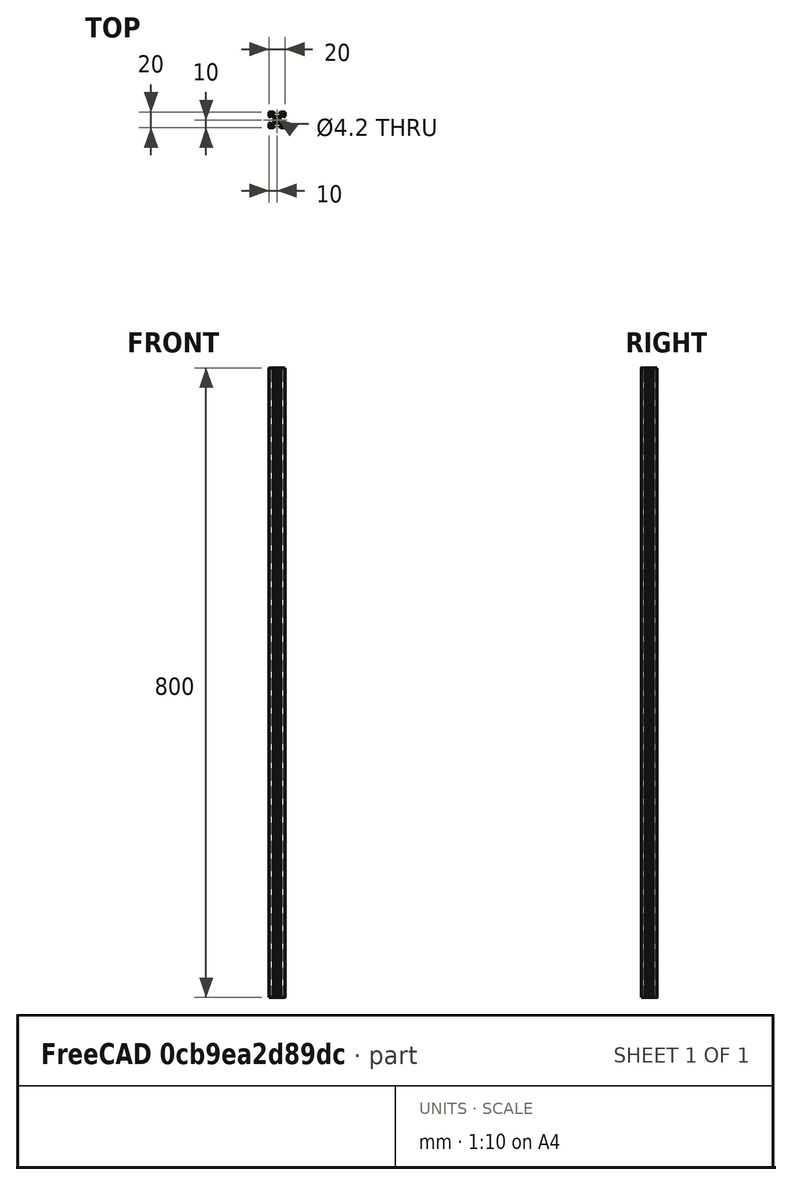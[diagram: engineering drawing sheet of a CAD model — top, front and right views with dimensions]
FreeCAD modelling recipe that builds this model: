
FCSTD DOCUMENT  (FreeCAD 0.19R)
Label: 2020-800
License: All rights reserved
LicenseURL: http://en.wikipedia.org/wiki/All_rights_reserved
objects: Sketcher::SketchObject×1, PartDesign::Pad×1, PartDesign::Body×1
note: 4 computed .brp shape members not serialized (recipe doc carries the construction recipe); baked Part::Feature solids carry a one-line shape summary decoded from their .brp

FEATURE [Sketcher::SketchObject] Sketch
  FullyConstrained = true
  MapMode = 5
  Support = -> [XY_Plane]
  sketch-geometry (65):
    g0: LineSegment StartX=-10 StartY=4.58 StartZ=0 EndX=-10 EndY=9.5 EndZ=0
    g1: LineSegment StartX=-9.5 StartY=10 StartZ=0 EndX=-4.58 EndY=10 EndZ=0
    g2: LineSegment StartX=-5.5 StartY=8.2 StartZ=0 EndX=-3.125 EndY=8.2 EndZ=0
    g3: LineSegment StartX=-8.2 StartY=5.5 StartZ=0 EndX=-8.2 EndY=3.125 EndZ=0
    g4: LineSegment StartX=-0.125 StartY=3.9 StartZ=0 EndX=-2.83934 EndY=3.9 EndZ=0
    g5: LineSegment StartX=-3.9 StartY=2.83934 StartZ=0 EndX=-3.9 EndY=0.125 EndZ=0
    g6: ArcOfCircle CenterX=0 CenterY=3.9 CenterZ=0 NormalX=0 NormalY=0 NormalZ=1 AngleXU=0 Radius=0.125 StartAngle=3.14159 EndAngle=6.28319
    g7: ArcOfCircle CenterX=-3.9 CenterY=0 CenterZ=0 NormalX=0 NormalY=0 NormalZ=1 AngleXU=0 Radius=0.125 StartAngle=4.71239 EndAngle=7.85398
    g8: ArcOfCircle CenterX=-9.5 CenterY=9.5 CenterZ=0 NormalX=0 NormalY=0 NormalZ=1 AngleXU=0 Radius=0.5 StartAngle=1.5708 EndAngle=3.14159
    g9: LineSegment StartX=-5.5 StartY=8.2 StartZ=0 EndX=-5.5 EndY=6.56066 EndZ=0
    g10: LineSegment StartX=-8.2 StartY=5.5 StartZ=0 EndX=-6.56066 EndY=5.5 EndZ=0
    g11: LineSegment StartX=-4.58 StartY=10 StartZ=0 EndX=-3.125 EndY=8.545 EndZ=0
    g12: LineSegment StartX=-3.125 StartY=8.545 StartZ=0 EndX=-3.125 EndY=8.2 EndZ=0
    g13: LineSegment StartX=-10 StartY=4.58 StartZ=0 EndX=-8.545 EndY=3.125 EndZ=0
    g14: LineSegment StartX=-8.545 StartY=3.125 StartZ=0 EndX=-8.2 EndY=3.125 EndZ=0
    g15: LineSegment StartX=-5.5 StartY=6.56066 StartZ=0 EndX=-2.83934 EndY=3.9 EndZ=0
    g16: LineSegment StartX=-6.56066 StartY=5.5 StartZ=0 EndX=-3.9 EndY=2.83934 EndZ=0
    g17: Circle CenterX=0 CenterY=0 CenterZ=0 NormalX=0 NormalY=0 NormalZ=1 AngleXU=0 Radius=2.1
    g18: LineSegment StartX=0.125 StartY=3.9 StartZ=0 EndX=2.83934 EndY=3.9 EndZ=0
    g19: LineSegment StartX=2.83934 StartY=3.9 StartZ=0 EndX=5.5 EndY=6.56066 EndZ=0
    g20: LineSegment StartX=5.5 StartY=6.56066 StartZ=0 EndX=5.5 EndY=8.2 EndZ=0
    g21: LineSegment StartX=3.125 StartY=8.2 StartZ=0 EndX=3.125 EndY=8.545 EndZ=0
    g22: LineSegment StartX=5.5 StartY=8.2 StartZ=0 EndX=3.125 EndY=8.2 EndZ=0
    g23: LineSegment StartX=4.58 StartY=10 StartZ=0 EndX=9.5 EndY=10 EndZ=0
    g24: ArcOfCircle CenterX=9.5 CenterY=9.5 CenterZ=0 NormalX=0 NormalY=0 NormalZ=1 AngleXU=0 Radius=0.5 StartAngle=1.9e-15 EndAngle=1.5708
    g25: LineSegment StartX=10 StartY=9.5 StartZ=0 EndX=10 EndY=4.58 EndZ=0
    g26: LineSegment StartX=10 StartY=4.58 StartZ=0 EndX=8.545 EndY=3.125 EndZ=0
    g27: LineSegment StartX=8.545 StartY=3.125 StartZ=0 EndX=8.2 EndY=3.125 EndZ=0
    g28: LineSegment StartX=8.2 StartY=3.125 StartZ=0 EndX=8.2 EndY=5.5 EndZ=0
    g29: LineSegment StartX=8.2 StartY=5.5 StartZ=0 EndX=6.56066 EndY=5.5 EndZ=0
    g30: LineSegment StartX=6.56066 StartY=5.5 StartZ=0 EndX=3.9 EndY=2.83934 EndZ=0
    g31: LineSegment StartX=3.9 StartY=2.83934 StartZ=0 EndX=3.9 EndY=0.125 EndZ=0
    g32: ArcOfCircle CenterX=3.9 CenterY=0 CenterZ=0 NormalX=0 NormalY=0 NormalZ=1 AngleXU=0 Radius=0.125 StartAngle=1.5708 EndAngle=4.71239
    g33: LineSegment StartX=3.9 StartY=-0.125 StartZ=0 EndX=3.9 EndY=-2.83934 EndZ=0
    g34: LineSegment StartX=3.9 StartY=-2.83934 StartZ=0 EndX=6.56066 EndY=-5.5 EndZ=0
    g35: LineSegment StartX=6.56066 StartY=-5.5 StartZ=0 EndX=8.2 EndY=-5.5 EndZ=0
    g36: LineSegment StartX=8.2 StartY=-5.5 StartZ=0 EndX=8.2 EndY=-3.125 EndZ=0
    g37: LineSegment StartX=8.2 StartY=-3.125 StartZ=0 EndX=8.545 EndY=-3.125 EndZ=0
    g38: LineSegment StartX=8.545 StartY=-3.125 StartZ=0 EndX=10 EndY=-4.58 EndZ=0
    g39: LineSegment StartX=10 StartY=-4.58 StartZ=0 EndX=10 EndY=-9.5 EndZ=0
    g40: ArcOfCircle CenterX=9.5 CenterY=-9.5 CenterZ=0 NormalX=0 NormalY=0 NormalZ=1 AngleXU=0 Radius=0.5 StartAngle=4.71239 EndAngle=6.28319
    g41: LineSegment StartX=9.5 StartY=-10 StartZ=0 EndX=4.58 EndY=-10 EndZ=0
    g42: LineSegment StartX=4.58 StartY=-10 StartZ=0 EndX=3.125 EndY=-8.545 EndZ=0
    g43: LineSegment StartX=2.83934 StartY=-3.9 StartZ=0 EndX=5.5 EndY=-6.56066 EndZ=0
    g44: LineSegment StartX=3.125 StartY=-8.545 StartZ=0 EndX=3.125 EndY=-8.2 EndZ=0
    g45: LineSegment StartX=3.125 StartY=-8.2 StartZ=0 EndX=5.5 EndY=-8.2 EndZ=0
    g46: LineSegment StartX=5.5 StartY=-8.2 StartZ=0 EndX=5.5 EndY=-6.56066 EndZ=0
    g47: ArcOfCircle CenterX=0 CenterY=-3.9 CenterZ=0 NormalX=0 NormalY=0 NormalZ=1 AngleXU=0 Radius=0.125 StartAngle=0 EndAngle=3.14159
    g48: LineSegment StartX=0.125 StartY=-3.9 StartZ=0 EndX=2.83934 EndY=-3.9 EndZ=0
    g49: LineSegment StartX=-0.125 StartY=-3.9 StartZ=0 EndX=-2.83934 EndY=-3.9 EndZ=0
    g50: LineSegment StartX=-3.9 StartY=-0.125 StartZ=0 EndX=-3.9 EndY=-2.83934 EndZ=0
    g51: LineSegment StartX=-3.9 StartY=-2.83934 StartZ=0 EndX=-6.56066 EndY=-5.5 EndZ=0
    g52: LineSegment StartX=-6.56066 StartY=-5.5 StartZ=0 EndX=-8.2 EndY=-5.5 EndZ=0
    g53: LineSegment StartX=-8.2 StartY=-5.5 StartZ=0 EndX=-8.2 EndY=-3.125 EndZ=0
    g54: LineSegment StartX=-8.2 StartY=-3.125 StartZ=0 EndX=-8.545 EndY=-3.125 EndZ=0
    g55: LineSegment StartX=-8.545 StartY=-3.125 StartZ=0 EndX=-10 EndY=-4.58 EndZ=0
    g56: LineSegment StartX=-10 StartY=-4.58 StartZ=0 EndX=-10 EndY=-9.5 EndZ=0
    g57: ArcOfCircle CenterX=-9.5 CenterY=-9.5 CenterZ=0 NormalX=0 NormalY=0 NormalZ=1 AngleXU=0 Radius=0.5 StartAngle=3.14159 EndAngle=4.71239
    g58: LineSegment StartX=-9.5 StartY=-10 StartZ=0 EndX=-4.58 EndY=-10 EndZ=0
    g59: LineSegment StartX=-4.58 StartY=-10 StartZ=0 EndX=-3.125 EndY=-8.545 EndZ=0
    g60: LineSegment StartX=-2.83934 StartY=-3.9 StartZ=0 EndX=-5.5 EndY=-6.56066 EndZ=0
    g61: LineSegment StartX=-5.5 StartY=-6.56066 StartZ=0 EndX=-5.5 EndY=-8.2 EndZ=0
    g62: LineSegment StartX=-5.5 StartY=-8.2 StartZ=0 EndX=-3.125 EndY=-8.2 EndZ=0
    g63: LineSegment StartX=-3.125 StartY=-8.545 StartZ=0 EndX=-3.125 EndY=-8.2 EndZ=0
    g64: LineSegment StartX=3.125 StartY=8.545 StartZ=0 EndX=4.58 EndY=10 EndZ=0
  constraints (194):
    c: Diameter(g17) = 4.2
    c: Radius(g32) = 0.125
    c: Coincident(g-1,g17)
    c: DistanceY(g57,g1) = 20
    c: DistanceX(g56,g39) = 20
    c: Radius(g57) = 0.5
    c: DistanceX(g56,g17) = 10
    c: DistanceY(g57,g17) = 10
    c: Distance(g5,g4) = 1.5
    c: DistanceY(g20,g23) = 1.8
    c: DistanceY(g18,g20) = 4.3
    c: DistanceX(g11,g21) = 6.25
    c: DistanceX(g1,g23) = 9.16
    c: DistanceX(g2,g20) = 11
    c: Coincident(g6,g18)
    c: Coincident(g6,g4)
    c: Coincident(g4,g15)
    c: Coincident(g18,g19)
    c: Coincident(g5,g16)
    c: Coincident(g16,g10)
    c: Coincident(g15,g9)
    c: Coincident(g12,g2)
    c: Coincident(g2,g9)
    c: Coincident(g12,g11)
    c: Coincident(g1,g11)
    c: Coincident(g23,g64)
    c: Coincident(g22,g21)
    c: Coincident(g64,g21)
    c: Coincident(g22,g20)
    c: Coincident(g19,g20)
    c: Coincident(g25,g26)
    c: Coincident(g27,g26)
    c: Coincident(g27,g28)
    c: Coincident(g28,g29)
    c: Coincident(g29,g30)
    c: Coincident(g0,g13)
    c: Coincident(g14,g13)
    c: Coincident(g14,g3)
    c: Coincident(g3,g10)
    c: Coincident(g5,g7)
    c: Coincident(g50,g7)
    c: Coincident(g51,g50)
    c: Coincident(g52,g51)
    c: Coincident(g52,g53)
    c: Coincident(g54,g53)
    c: Coincident(g55,g54)
    c: Coincident(g56,g55)
    c: Coincident(g58,g59)
    c: Coincident(g63,g59)
    c: Coincident(g62,g63)
    c: Coincident(g62,g61)
    c: Coincident(g60,g61)
    c: Coincident(g49,g60)
    c: Coincident(g47,g49)
    c: Coincident(g48,g47)
    c: Coincident(g48,g43)
    c: Coincident(g46,g43)
    c: Coincident(g45,g46)
    c: Coincident(g45,g44)
    c: Coincident(g42,g44)
    c: Coincident(g41,g42)
    c: Coincident(g39,g38)
    c: Coincident(g38,g37)
    c: Coincident(g37,g36)
    c: Coincident(g35,g36)
    c: Coincident(g34,g35)
    c: Coincident(g34,g33)
    c: Coincident(g31,g30)
    c: Coincident(g33,g32)
    c: Coincident(g32,g31)
    c: Vertical(g0)
    c: Horizontal(g1)
    c: Equal(g0,g1)
    c: Horizontal(g4)
    c: PointOnObject(g6,g-2)
    c: Horizontal(g18)
    c: Horizontal(g4,g6)
    c: Horizontal(g6,g6)
    c: Parallel(g13,g11)
    c: Horizontal(g14)
    c: Vertical(g12)
    c: Equal(g14,g12)
    c: Vertical(g3)
    c: Horizontal(g2)
    c: Equal(g3,g2)
    c: Equal(g10,g9)
    c: Horizontal(g10)
    c: Vertical(g9)
    c: Parallel(g16,g15)
    c: Equal(g13,g11)
    c: Tangent(g8,g0) = 1.5708
    c: PointOnObject(g7,g-1)
    c: Vertical(g5)
    c: Vertical(g50)
    c: Vertical(g7,g7)
    c: Vertical(g7,g5)
    c: Horizontal(g52)
    c: Vertical(g53)
    c: Horizontal(g54)
    c: Vertical(g56)
    c: Equal(g50,g5)
    c: Equal(g51,g16)
    c: Perpendicular(g16,g51)
    c: Equal(g52,g10)
    c: Equal(g53,g3)
    c: Equal(g54,g14)
    c: Equal(g55,g13)
    c: Perpendicular(g55,g13)
    c: Equal(g56,g0)
    c: Tangent(g57,g56) = -1.5708
    c: Tangent(g57,g58) = -1.5708
    c: Tangent(g8,g1) = 1.5708
    c: Equal(g57,g8)
    c: Horizontal(g58)
    c: Equal(g58,g56)
    c: Equal(g55,g59)
    c: Parallel(g55,g59)
    c: Vertical(g63)
    c: Equal(g63,g54)
    c: Horizontal(g62)
    c: Vertical(g61)
    c: Equal(g61,g52)
    c: Equal(g60,g51)
    c: Parallel(g60,g51)
    c: PointOnObject(g47,g-2)
    c: Horizontal(g47,g47)
    c: Horizontal(g47,g47)
    c: Horizontal(g49)
    c: Equal(g49,g50)
    c: Horizontal(g48)
    c: Vertical(g46)
    c: Perpendicular(g60,g43)
    c: Equal(g43,g60)
    c: Equal(g46,g61)
    c: Horizontal(g45)
    c: Equal(g45,g62)
    c: Vertical(g44)
    c: Equal(g44,g63)
    c: Perpendicular(g42,g59)
    c: Equal(g42,g59)
    c: Horizontal(g41)
    c: Equal(g58,g41)
    c: Tangent(g40,g41) = 1.5708
    c: Tangent(g40,g39) = 1.5708
    c: Equal(g57,g40)
    c: Vertical(g39)
    c: Equal(g41,g39)
    c: Parallel(g42,g38)
    c: Equal(g42,g38)
    c: Horizontal(g37)
    c: Equal(g44,g37)
    c: Vertical(g36)
    c: Equal(g45,g36)
    c: Horizontal(g35)
    c: Equal(g35,g46)
    c: Parallel(g43,g34)
    c: Equal(g43,g34)
    c: PointOnObject(g32,g-1)
    c: Vertical(g33)
    c: Vertical(g32,g31)
    c: Vertical(g31,g32)
    c: Equal(g48,g33)
    c: Equal(g47,g7)
    c: Equal(g7,g6)
    c: Vertical(g31)
    c: Equal(g33,g31)
    c: Equal(g4,g5)
    c: Equal(g4,g18)
    c: Parallel(g30,g19)
    c: Equal(g30,g19)
    c: Horizontal(g29)
    c: Vertical(g20)
    c: Equal(g35,g29)
    c: Equal(g29,g20)
    c: Horizontal(g22)
    c: Equal(g22,g2)
    c: Vertical(g21)
    c: Equal(g11,g64)
    c: Horizontal(g23)
    c: Equal(g1,g23)
    c: Vertical(g28)
    c: Equal(g28,g36)
    c: Horizontal(g27)
    c: Equal(g27,g37)
    c: Perpendicular(g38,g26)
    c: Equal(g38,g26)
    c: Vertical(g25)
    c: Equal(g39,g25)
    c: Tangent(g24,g23) = 1.5708
    c: Tangent(g24,g25) = 1.5708
    c: Vertical(g25,g38)
    c: Horizontal(g2,g21)
    c: Vertical(g10,g51)
    c: Angle(g64,g11) = 1.5708
FEATURE [PartDesign::Pad] Pad
  Direction = (1,1,1)
  Length = 800
  Length2 = 100
  Profile = -> Sketch
  Type = 0
FEATURE [PartDesign::Body] Body  label="2020-800"
  Group = -> [Sketch,Pad]
  Origin = -> Origin
  Tip = -> Pad
